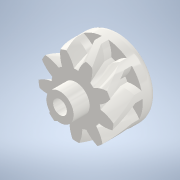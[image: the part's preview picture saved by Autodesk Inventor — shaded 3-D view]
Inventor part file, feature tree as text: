
AUTODESK INVENTOR PART (.ipt)
format: ipt  version: 2022 (Build 260153070, 153G)  size: 455,680 bytes
history: native  units: mm (DEFAULTED — no unit token found)
features: sketch x6, extrude x5, plane x3, other x3, fillet x1, projected_geometry x1
ambient origin geometry x8: Origin, YZ Plane, XZ Plane, XY Plane, X Axis, Y Axis, Z Axis, Center Point
bodies: Solid1 (feature_tree)
feature tree (19):
  extrude  "Extrusion1"  Depth=3.0mm TaperAngle=0.0deg
  plane  "Work Plane2"
  plane  "Work Plane8"
  plane  "Work Plane9"
  other  "Spur Gear"
  extrude  "Extrusion2"  Depth=10.0mm TaperAngle=0.0deg
  extrude  "Extrusion3"  Depth=3.490659mm TaperAngle=0.0deg
  fillet  "Fillet1"  [1 undecoded]
  extrude  "Extrusion5"  Depth=20.0mm
  extrude  "Extrusion4"  TaperAngle=0.0deg  [1 undecoded]
  sketch  "Sketch1"  dims[d0=10.350115mm d1=3.0mm d2=0.0mm]
  sketch  "Sketch2"  dims[d3=7.9mm d4=10.0mm d5=0.0mm]
  other  "Srf1"
  sketch  "Sketch3"  dims[d16=20.0mm d17=0.0mm d34=3.490659mm d39=0.0mm]
  projected_geometry  "Projected Loop1"
  sketch  "Sketch4"  dims[d41=0.0mm d43=20.0mm]
  sketch  "Sketch5"  dims[d46=20.0mm d47=0.0mm d48=0.0mm]
  sketch  "Sketch6"  dims[d52=1.5mm d53=1.0mm d54=0.0mm d55=6.15mm d56=2.0mm d57=0.0mm d58=1.0mm d59=1.9mm d60=2.9mm d61=0.0mm d62=2.2mm d63=0.0mm d64=2.0mm d65=0.0mm d66=3.75mm]
  other  "Pitch Diameter"
note: 2 required parameter values undecoded (feature->parameter linkage not recoverable at this tier; creation-order binding heuristic only, values carry confidence <= 0.55)
